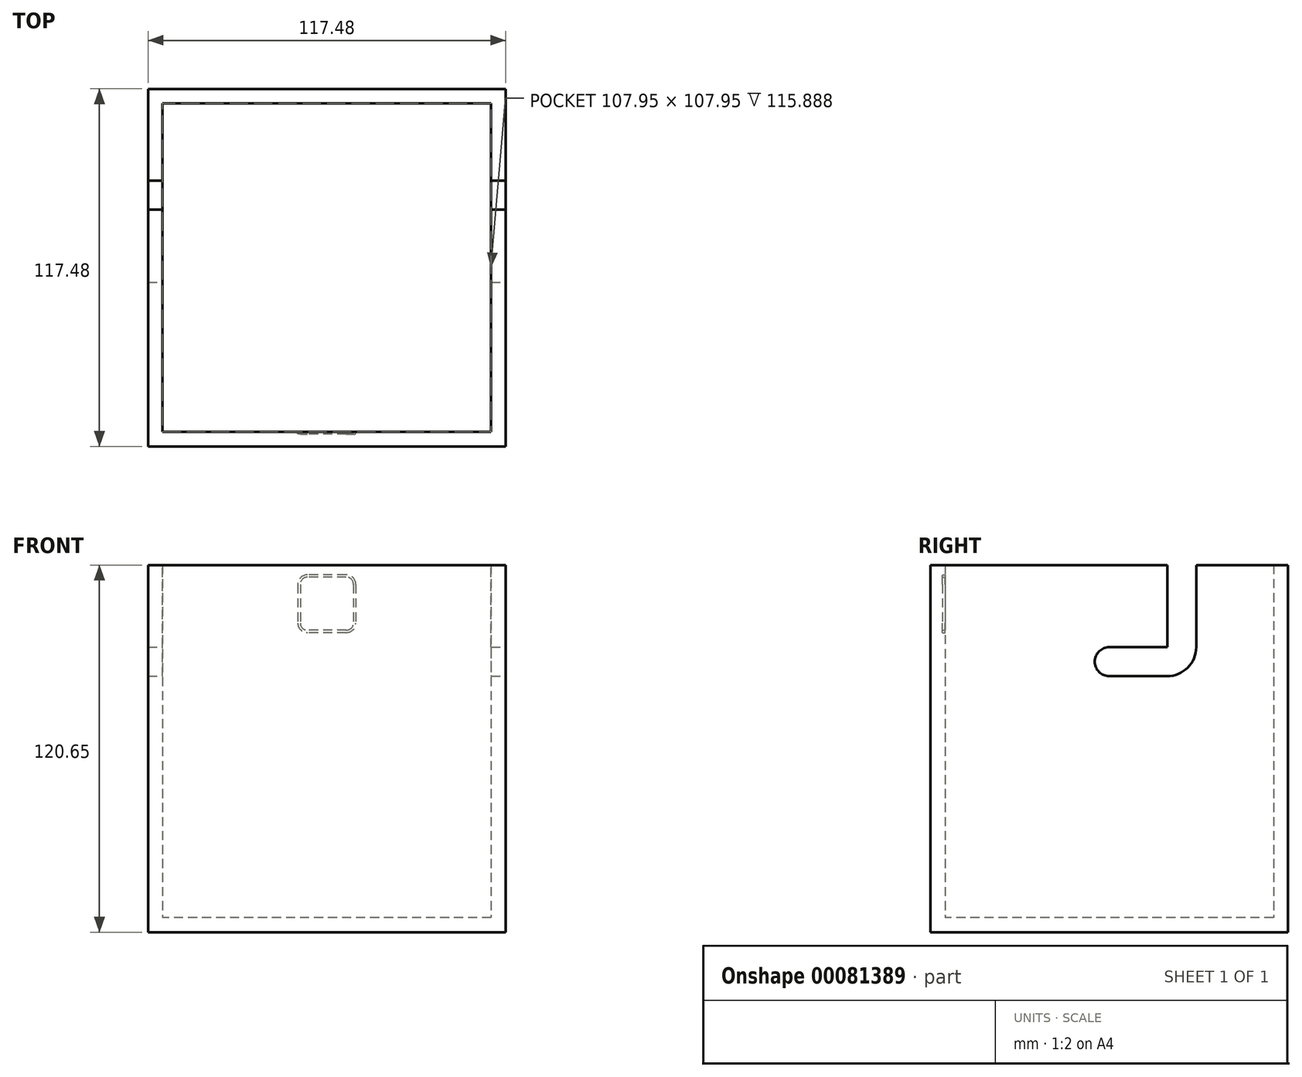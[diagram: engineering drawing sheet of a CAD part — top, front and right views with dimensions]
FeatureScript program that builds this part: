
annotation { "Feature Type Name" : "Feature", "Feature Type Description" : "" }
export const myFeature = defineFeature(function(context is Context, id is Id, definition is map)
    precondition{}
    {
        {
            var Q0;
            Q0=qCreatedBy(makeId("Top.planeOp"),FACE);
            var sketch = newSketch(context, id + "F0", { "sketchPlane" : qUnion([Q0])});
            skLineSegment(sketch, "E0.bottom", {"start": v(58.74, 58.74) * mm, "end": v(-58.74, 58.74) * mm});
            skLineSegment(sketch, "E0.top", {"start": v(58.74, -58.74) * mm, "end": v(-58.74, -58.74) * mm});
            skLineSegment(sketch, "E0.left", {"start": v(58.74, 58.74) * mm, "end": v(58.74, -58.74) * mm});
            skLineSegment(sketch, "E0.right", {"start": v(-58.74, 58.74) * mm, "end": v(-58.74, -58.74) * mm});
            skPoint(sketch, "E0.middle", {"position": v(0, 0) * mm});
            skSolve(sketch);
        }
        {
            var Q0;
            Q0=makeQuery(id+"F0.imprint","IMPRINT",FACE,{"disambiguationData":[TD([[makeQuery(id+"F0.imprint","IMPRINT",EDGE,{"derivedFrom":sQuery(id+"F0.wireOp",EDGE,"E0.bottom")}),1.0]])]});
            extrude(context, id + "F1", {"entities" : qUnion([Q0]), "depth" : 120.65 * mm});
        }
        {
            var Q0;
            Q0=makeQuery(id+"F1.opExtrude","CAP_FACE",FACE,{"disambiguationData":[OSD([sQuery(id+"F0.wireOp",EDGE,"E0.bottom"),sQuery(id+"F0.wireOp",EDGE,"E0.top"),sQuery(id+"F0.wireOp",EDGE,"E0.left"),sQuery(id+"F0.wireOp",EDGE,"E0.right")])],"isStart":false});
            shell(context, id + "F2", {"entities" : qUnion([Q0]), "thickness" : 4.76 * mm});
        }
        {
            var Q0;
            Q0=makeQuery(id+"F1.opExtrude","SWEPT_FACE",FACE,{"disambiguationData":[OSD([sQuery(id+"F0.wireOp",EDGE,"E0.left")])]});
            var sketch = newSketch(context, id + "F3", { "sketchPlane" : qUnion([Q0])});
            skPoint(sketch, "E1", {"position": v(0, 88.9) * mm});
            skSolve(sketch);
        }
        {
            var Q0;
            Q0=sQuery(id+"F3.wireOp",VERTEX,"E1");
            var Q1;
            Q1=makeQuery(id+"F1.opExtrude","SWEPT_BODY",BODY,{"disambiguationData":[OSD([sQuery(id+"F0.wireOp",EDGE,"E0.bottom"),sQuery(id+"F0.wireOp",EDGE,"E0.top"),sQuery(id+"F0.wireOp",EDGE,"E0.left"),sQuery(id+"F0.wireOp",EDGE,"E0.right")])]});
            hole(context, id + "F4", {"style" : HoleStyle.SIMPLE, "endStyle" : HoleEndStyle.THROUGH, "holeDiameter" : 9.52 * mm, "locations" : qUnion([Q0]), "scope" : qUnion([Q1]), "isTappedThrough" : true});
        }
        {
            var Q0;
            Q0=makeQuery(id+"F2.opShell","OFFSET_FACE",FACE,{"disambiguationData":[OSD([sQuery(id+"F0.wireOp",EDGE,"E0.top")])]});
            var sketch = newSketch(context, id + "F5", { "sketchPlane" : qUnion([Q0])});
            skLineSegment(sketch, "E2.bottom", {"start": v(-6.35, 117.48) * mm, "end": v(6.35, 117.48) * mm});
            skLineSegment(sketch, "E2.top", {"start": v(-6.35, 98.43) * mm, "end": v(6.35, 98.43) * mm});
            skLineSegment(sketch, "E2.left", {"start": v(-9.53, 114.3) * mm, "end": v(-9.53, 101.6) * mm});
            skLineSegment(sketch, "E2.right", {"start": v(9.53, 114.3) * mm, "end": v(9.53, 101.6) * mm});
            skPoint(sketch, "E3.visualSharp", {"position": v(9.52, 117.48) * mm});
            skArc(sketch, "E3.filletArc", {"start": v(9.52, 114.3) * mm, "mid": v(8.6, 116.55) * mm, "end": v(6.35, 117.48) * mm});
            skPoint(sketch, "E4.visualSharp", {"position": v(9.53, 98.43) * mm});
            skArc(sketch, "E4.filletArc", {"start": v(6.35, 98.42) * mm, "mid": v(8.6, 99.35) * mm, "end": v(9.53, 101.6) * mm});
            skPoint(sketch, "E5.visualSharp", {"position": v(-9.53, 98.43) * mm});
            skArc(sketch, "E5.filletArc", {"start": v(-9.53, 101.6) * mm, "mid": v(-8.6, 99.35) * mm, "end": v(-6.35, 98.42) * mm});
            skPoint(sketch, "E6.visualSharp", {"position": v(-9.53, 117.48) * mm});
            skArc(sketch, "E6.filletArc", {"start": v(-6.35, 117.48) * mm, "mid": v(-8.6, 116.55) * mm, "end": v(-9.53, 114.3) * mm});
            skLineSegment(sketch, "E7", {"start": v(0, 120.65) * mm, "end": v(0, 101.6) * mm});
            skPoint(sketch, "E7.endSnap0", {"position": v(0, 120.65) * mm});
            skLineSegment(sketch, "E8.0", {"start": v(-6.35, 116.68) * mm, "end": v(6.35, 116.68) * mm});
            skLineSegment(sketch, "E8.1", {"start": v(-8.73, 114.3) * mm, "end": v(-8.73, 101.6) * mm});
            skLineSegment(sketch, "E8.2", {"start": v(-6.35, 99.22) * mm, "end": v(6.35, 99.22) * mm});
            skLineSegment(sketch, "E8.3", {"start": v(8.73, 114.3) * mm, "end": v(8.73, 101.6) * mm});
            skPoint(sketch, "E9.visualSharp", {"position": v(8.73, 116.68) * mm});
            skArc(sketch, "E9.filletArc", {"start": v(8.73, 114.3) * mm, "mid": v(8.03, 115.98) * mm, "end": v(6.35, 116.68) * mm});
            skPoint(sketch, "E10.visualSharp", {"position": v(8.73, 99.22) * mm});
            skArc(sketch, "E10.filletArc", {"start": v(6.35, 99.22) * mm, "mid": v(8.03, 99.92) * mm, "end": v(8.73, 101.6) * mm});
            skPoint(sketch, "E11.visualSharp", {"position": v(-8.73, 99.22) * mm});
            skArc(sketch, "E11.filletArc", {"start": v(-8.73, 101.6) * mm, "mid": v(-8.03, 99.92) * mm, "end": v(-6.35, 99.22) * mm});
            skPoint(sketch, "E12.visualSharp", {"position": v(-8.73, 116.68) * mm});
            skArc(sketch, "E12.filletArc", {"start": v(-6.35, 116.68) * mm, "mid": v(-8.03, 115.98) * mm, "end": v(-8.73, 114.3) * mm});
            skSolve(sketch);
        }
        {
            var Q0;
            Q0=makeQuery(id+"F5.imprint","IMPRINT",FACE,{"disambiguationData":[TD([[makeQuery(id+"F5.imprint","IMPRINT",EDGE,{"derivedFrom":sQuery(id+"F5.wireOp",EDGE,"E2.top")}),1.0]])]});
            var Q1;
            Q1=sQuery(id+"F5.wireOp",EDGE,"E11.filletArc");
            var Q2;
            Q2=sQuery(id+"F5.wireOp",EDGE,"E2.right");
            var Q3;
            Q3=sQuery(id+"F5.wireOp",EDGE,"E3.filletArc");
            var Q4;
            Q4=sQuery(id+"F5.wireOp",EDGE,"E2.bottom");
            var Q5;
            Q5=sQuery(id+"F5.wireOp",EDGE,"E6.filletArc");
            var Q6;
            Q6=sQuery(id+"F5.wireOp",EDGE,"E2.left");
            var Q7;
            Q7=sQuery(id+"F5.wireOp",EDGE,"E5.filletArc");
            var Q8;
            Q8=sQuery(id+"F5.wireOp",EDGE,"E2.top");
            var Q9;
            Q9=sQuery(id+"F5.wireOp",EDGE,"E4.filletArc");
            var Q10;
            Q10=sQuery(id+"F5.wireOp",EDGE,"E8.3");
            var Q11;
            Q11=sQuery(id+"F5.wireOp",EDGE,"E9.filletArc");
            var Q12;
            Q12=sQuery(id+"F5.wireOp",EDGE,"E8.0");
            var Q13;
            Q13=sQuery(id+"F5.wireOp",EDGE,"E12.filletArc");
            var Q14;
            Q14=sQuery(id+"F5.wireOp",EDGE,"E8.1");
            var Q15;
            Q15=sQuery(id+"F5.wireOp",EDGE,"E8.2");
            var Q16;
            Q16=sQuery(id+"F5.wireOp",EDGE,"E10.filletArc");
            extrude(context, id + "F6", {"entities" : qUnion([Q0]), "surfaceEntities" : qUnion([Q1, Q2, Q3, Q4, Q5, Q6, Q7, Q8, Q9, Q10, Q11, Q12, Q13, Q14, Q15, Q16]), "oppositeDirection" : true, "depth" : 0.8 * mm});
        }
        {
            var Q0;
            Q0=makeQuery(id+"F6.opExtrude","SWEPT_BODY",BODY,{"disambiguationData":[OSD([sQuery(id+"F5.wireOp",EDGE,"E2.bottom"),sQuery(id+"F5.wireOp",EDGE,"E2.top"),sQuery(id+"F5.wireOp",EDGE,"E2.left"),sQuery(id+"F5.wireOp",EDGE,"E2.right"),sQuery(id+"F5.wireOp",EDGE,"E3.filletArc"),sQuery(id+"F5.wireOp",EDGE,"E4.filletArc"),sQuery(id+"F5.wireOp",EDGE,"E5.filletArc"),sQuery(id+"F5.wireOp",EDGE,"E6.filletArc"),sQuery(id+"F5.wireOp",EDGE,"E8.0"),sQuery(id+"F5.wireOp",EDGE,"E8.1"),sQuery(id+"F5.wireOp",EDGE,"E8.2"),sQuery(id+"F5.wireOp",EDGE,"E8.3"),sQuery(id+"F5.wireOp",EDGE,"E9.filletArc"),sQuery(id+"F5.wireOp",EDGE,"E10.filletArc"),sQuery(id+"F5.wireOp",EDGE,"E11.filletArc"),sQuery(id+"F5.wireOp",EDGE,"E12.filletArc")])]});
            var Q1;
            Q1=makeQuery(id+"F1.opExtrude","SWEPT_BODY",BODY,{"disambiguationData":[OSD([sQuery(id+"F0.wireOp",EDGE,"E0.bottom"),sQuery(id+"F0.wireOp",EDGE,"E0.top"),sQuery(id+"F0.wireOp",EDGE,"E0.left"),sQuery(id+"F0.wireOp",EDGE,"E0.right")])]});
            booleanBodies(context, id + "F7", {"operationType" : BooleanOperationType.SUBTRACTION, "tools" : qUnion([Q0]), "targets" : qUnion([Q1])});
        }
        {
            var Q0;
            {var subQ0=sQuery(id+"F0.wireOp",EDGE,"E0.left");Q0=makeQuery(id+"F3.imprint","IMPRINT",FACE,{"disambiguationData":[TD([[makeQuery(id+"F3.imprint","IMPRINT",EDGE,{"derivedFrom":makeQuery(id+"F1.opExtrude","CAP_EDGE",EDGE,{"disambiguationData":[OSD([subQ0])],"isStart":true})}),-1.0]])]});}
            var sketch = newSketch(context, id + "F8", { "sketchPlane" : qUnion([Q0])});
            skLineSegment(sketch, "E13", {"start": v(0, 84.14) * mm, "end": v(19.05, 84.14) * mm});
            skLineSegment(sketch, "E14", {"start": v(28.57, 93.66) * mm, "end": v(28.57, 120.65) * mm});
            skPoint(sketch, "E15.visualSharp", {"position": v(28.57, 84.14) * mm});
            skArc(sketch, "E15.filletArc", {"start": v(19.05, 84.14) * mm, "mid": v(25.79, 86.93) * mm, "end": v(28.57, 93.66) * mm});
            skLineSegment(sketch, "E16.0", {"start": v(19.05, 93.66) * mm, "end": v(19.05, 120.65) * mm});
            skLineSegment(sketch, "E16.1", {"start": v(19.05, 93.66) * mm, "end": v(19.05, 93.66) * mm});
            skLineSegment(sketch, "E16.2", {"start": v(0, 93.66) * mm, "end": v(19.05, 93.66) * mm});
            skLineSegment(sketch, "E17", {"start": v(28.57, 120.65) * mm, "end": v(19.05, 120.65) * mm});
            skArc(sketch, "E18", {"start": v(0, 84.14) * mm, "mid": v(4.76, 88.9) * mm, "end": v(0, 93.66) * mm});
            skSolve(sketch);
        }
        {
            var Q0;
            {var subQ3=sQuery(id+"F8.wireOp",EDGE,"E17");Q0=makeQuery(id+"F8.imprint","IMPRINT",FACE,{"disambiguationData":[TD([[makeQuery(id+"F8.imprint","IMPRINT",EDGE,{"derivedFrom":subQ3}),1.0]])]});}
            var Q1;
            Q1=sQuery(id+"F8.wireOp",EDGE,"E14");
            var Q2;
            Q2=sQuery(id+"F8.wireOp",EDGE,"E17");
            var Q3;
            Q3=sQuery(id+"F8.wireOp",EDGE,"E16.0");
            var Q4;
            Q4=sQuery(id+"F8.wireOp",EDGE,"E16.2");
            var Q5;
            Q5=sQuery(id+"F8.wireOp",EDGE,"E13");
            var Q6;
            Q6=sQuery(id+"F8.wireOp",EDGE,"E15.filletArc");
            var Q7;
            Q7=sQuery(id+"F8.wireOp",EDGE,"E18");
            var Q8;
            Q8=makeQuery(id+"F1.opExtrude","SWEPT_FACE",FACE,{"disambiguationData":[OSD([sQuery(id+"F0.wireOp",EDGE,"E0.right")])]});
            extrude(context, id + "F9", {"entities" : qUnion([Q0]), "surfaceEntities" : qUnion([Q1, Q2, Q3, Q4, Q5, Q6, Q7]), "endBound" : BoundingType.UP_TO_SURFACE, "oppositeDirection" : true, "endBoundEntityFace" : qUnion([Q8]), "depth" : 25.4 * mm});
        }
        {
            var Q0;
            Q0=makeQuery(id+"F9.opExtrude","SWEPT_BODY",BODY,{"disambiguationData":[OSD([sQuery(id+"F8.wireOp",EDGE,"E13"),sQuery(id+"F8.wireOp",EDGE,"E14"),sQuery(id+"F8.wireOp",EDGE,"E15.filletArc"),sQuery(id+"F8.wireOp",EDGE,"E16.0"),sQuery(id+"F8.wireOp",EDGE,"E16.2"),sQuery(id+"F8.wireOp",EDGE,"E17"),sQuery(id+"F8.wireOp",EDGE,"E18")])]});
            var Q1;
            Q1=makeQuery(id+"F1.opExtrude","SWEPT_BODY",BODY,{"disambiguationData":[OSD([sQuery(id+"F0.wireOp",EDGE,"E0.bottom"),sQuery(id+"F0.wireOp",EDGE,"E0.top"),sQuery(id+"F0.wireOp",EDGE,"E0.left"),sQuery(id+"F0.wireOp",EDGE,"E0.right")])]});
            booleanBodies(context, id + "F10", {"operationType" : BooleanOperationType.SUBTRACTION, "tools" : qUnion([Q0]), "targets" : qUnion([Q1])});
        }
    });
